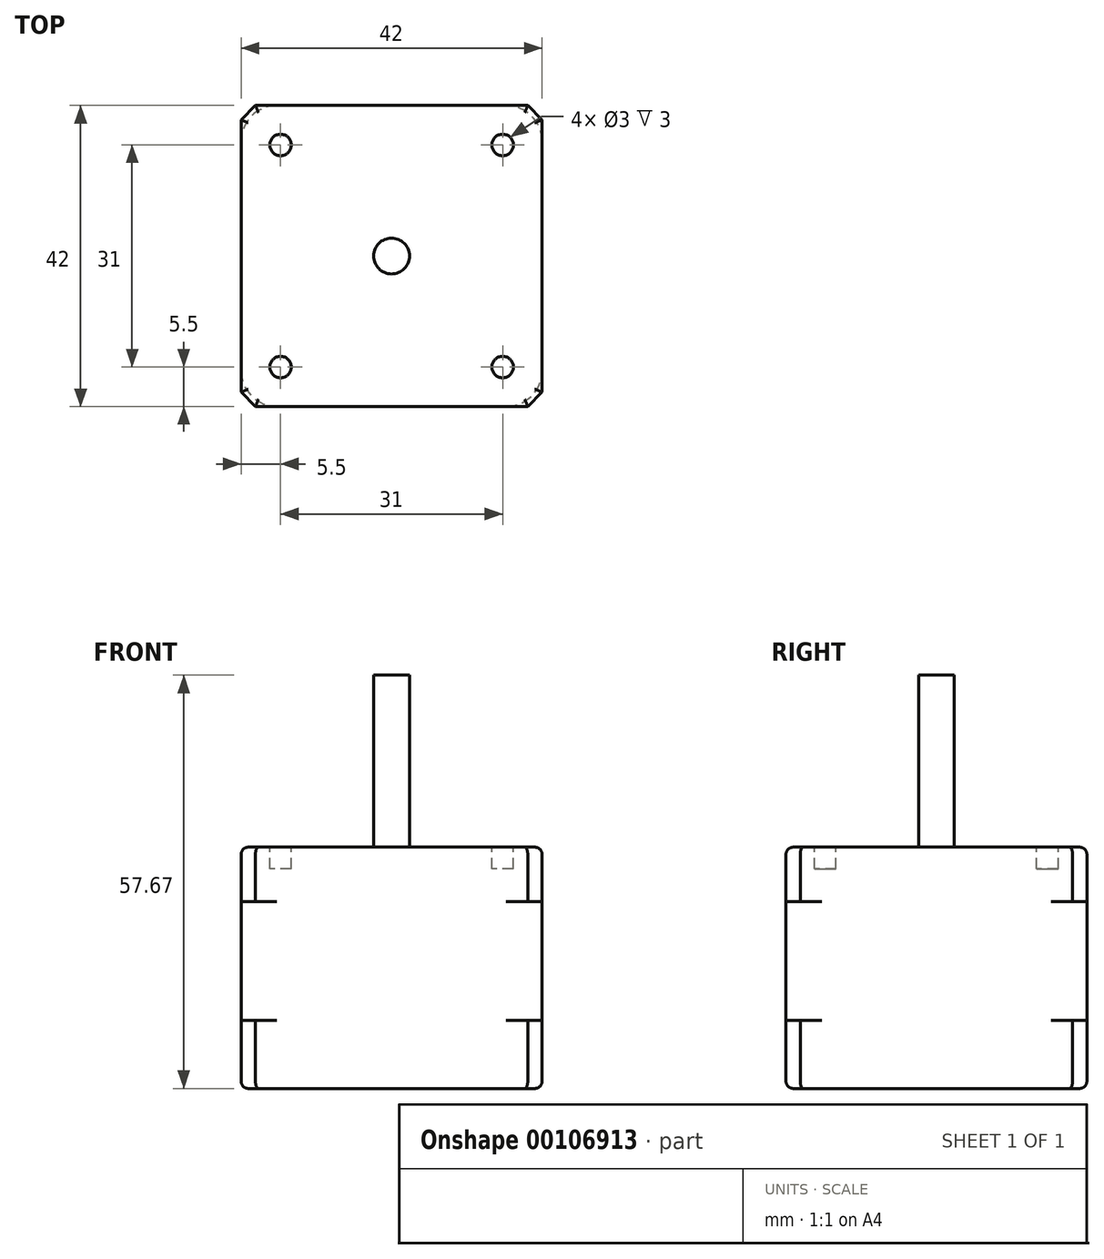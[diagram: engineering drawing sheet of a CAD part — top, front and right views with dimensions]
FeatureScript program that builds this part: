
annotation { "Feature Type Name" : "Feature", "Feature Type Description" : "" }
export const myFeature = defineFeature(function(context is Context, id is Id, definition is map)
    precondition{}
    {
        {
            var Q0;
            Q0=qCreatedBy(makeId("Top.planeOp"),FACE);
            var sketch = newSketch(context, id + "F0", { "sketchPlane" : qUnion([Q0])});
            skLineSegment(sketch, "E0.bottom", {"start": v(21, -21) * mm, "end": v(-21, -21) * mm});
            skLineSegment(sketch, "E0.top", {"start": v(21, 21) * mm, "end": v(-21, 21) * mm});
            skLineSegment(sketch, "E0.left", {"start": v(21, -21) * mm, "end": v(21, 21) * mm});
            skLineSegment(sketch, "E0.right", {"start": v(-21, -21) * mm, "end": v(-21, 21) * mm});
            skPoint(sketch, "E0.middle", {"position": v(0, 0) * mm});
            skSolve(sketch);
        }
        {
            var Q0;
            Q0 = qSketchRegion(id + "F0", true);
            extrude(context, id + "F1", {"entities" : qUnion([Q0]), "depth" : 9.5 * mm});
        }
        {
            var Q0;
            Q0=makeQuery(id+"F1.opExtrude","CAP_FACE",FACE,{"disambiguationData":[OSD([sQuery(id+"F0.wireOp",EDGE,"E0.bottom"),sQuery(id+"F0.wireOp",EDGE,"E0.top"),sQuery(id+"F0.wireOp",EDGE,"E0.left"),sQuery(id+"F0.wireOp",EDGE,"E0.right")])],"isStart":false});
            var sketch = newSketch(context, id + "F2", { "sketchPlane" : qUnion([Q0])});
            skLineSegment(sketch, "E1.bottom", {"start": v(16, -21) * mm, "end": v(-16, -21) * mm});
            skLineSegment(sketch, "E1.top", {"start": v(16, 21) * mm, "end": v(-16, 21) * mm});
            skLineSegment(sketch, "E1.left", {"start": v(21, -16) * mm, "end": v(21, 16) * mm});
            skLineSegment(sketch, "E1.right", {"start": v(-21, -16) * mm, "end": v(-21, 16) * mm});
            skPoint(sketch, "E1.middle", {"position": v(0, 0) * mm});
            skPoint(sketch, "E2.visualSharp", {"position": v(-21, 21) * mm});
            skArc(sketch, "E2.filletArc", {"start": v(-16, 21) * mm, "mid": v(-19.54, 19.54) * mm, "end": v(-21, 16) * mm});
            skPoint(sketch, "E3.visualSharp", {"position": v(-21, -21) * mm});
            skArc(sketch, "E3.filletArc", {"start": v(-21, -16) * mm, "mid": v(-19.54, -19.54) * mm, "end": v(-16, -21) * mm});
            skPoint(sketch, "E4.visualSharp", {"position": v(21, -21) * mm});
            skArc(sketch, "E4.filletArc", {"start": v(16, -21) * mm, "mid": v(19.54, -19.54) * mm, "end": v(21, -16) * mm});
            skPoint(sketch, "E5.visualSharp", {"position": v(21, 21) * mm});
            skArc(sketch, "E5.filletArc", {"start": v(21, 16) * mm, "mid": v(19.54, 19.54) * mm, "end": v(16, 21) * mm});
            skSolve(sketch);
        }
        {
            var Q0;
            Q0 = qSketchRegion(id + "F2", true);
            extrude(context, id + "F3", {"entities" : qUnion([Q0]), "operationType" : NewBodyOperationType.ADD, "depth" : 16.57 * mm});
        }
        {
            var Q0;
            Q0=makeQuery(id+"F3.opExtrude","CAP_FACE",FACE,{"disambiguationData":[OSD([sQuery(id+"F2.wireOp",EDGE,"E1.bottom"),sQuery(id+"F2.wireOp",EDGE,"E1.top"),sQuery(id+"F2.wireOp",EDGE,"E1.left"),sQuery(id+"F2.wireOp",EDGE,"E1.right"),sQuery(id+"F2.wireOp",EDGE,"E2.filletArc"),sQuery(id+"F2.wireOp",EDGE,"E3.filletArc"),sQuery(id+"F2.wireOp",EDGE,"E4.filletArc"),sQuery(id+"F2.wireOp",EDGE,"E5.filletArc")])],"isStart":false});
            var sketch = newSketch(context, id + "F4", { "sketchPlane" : qUnion([Q0])});
            skLineSegment(sketch, "E6.bottom", {"start": v(21, -21) * mm, "end": v(-21, -21) * mm});
            skLineSegment(sketch, "E6.top", {"start": v(21, 21) * mm, "end": v(-21, 21) * mm});
            skLineSegment(sketch, "E6.left", {"start": v(21, -21) * mm, "end": v(21, 21) * mm});
            skLineSegment(sketch, "E6.right", {"start": v(-21, -21) * mm, "end": v(-21, 21) * mm});
            skPoint(sketch, "E6.middle", {"position": v(0, 0) * mm});
            skSolve(sketch);
        }
        {
            var Q0;
            Q0 = qSketchRegion(id + "F4", true);
            extrude(context, id + "F5", {"entities" : qUnion([Q0]), "operationType" : NewBodyOperationType.ADD, "depth" : 7.6 * mm});
        }
        {
            var Q0;
            Q0=makeQuery(id+"F5.opExtrude","CAP_FACE",FACE,{"disambiguationData":[OSD([sQuery(id+"F4.wireOp",EDGE,"E6.bottom"),sQuery(id+"F4.wireOp",EDGE,"E6.top"),sQuery(id+"F4.wireOp",EDGE,"E6.left"),sQuery(id+"F4.wireOp",EDGE,"E6.right")])],"isStart":false});
            var sketch = newSketch(context, id + "F6", { "sketchPlane" : qUnion([Q0])});
            skLineSegment(sketch, "E7.bottom", {"start": v(15.5, -15.5) * mm, "end": v(14, -15.5) * mm});
            skLineSegment(sketch, "E7.top", {"start": v(15.5, 15.5) * mm, "end": v(14, 15.5) * mm});
            skLineSegment(sketch, "E7.left", {"start": v(15.5, -15.5) * mm, "end": v(15.5, -14) * mm});
            skLineSegment(sketch, "E7.right", {"start": v(-15.5, -15.5) * mm, "end": v(-15.5, -14) * mm});
            skPoint(sketch, "E7.middle", {"position": v(0, 0) * mm});
            skCircle(sketch, "E8", {"center": v(-15.5, 15.5) * mm, "radius": 1.5 * mm});
            skCircle(sketch, "E9", {"center": v(15.5, 15.5) * mm, "radius": 1.5 * mm});
            skCircle(sketch, "E10", {"center": v(-15.5, -15.5) * mm, "radius": 1.5 * mm});
            skCircle(sketch, "E11", {"center": v(15.5, -15.5) * mm, "radius": 1.5 * mm});
            skLineSegment(sketch, "E12.trimOffspring", {"start": v(-15.5, 14) * mm, "end": v(-15.5, 15.5) * mm});
            skLineSegment(sketch, "E13.trimOffspring", {"start": v(-14, 15.5) * mm, "end": v(-15.5, 15.5) * mm});
            skLineSegment(sketch, "E14.trimOffspring", {"start": v(15.5, 14) * mm, "end": v(15.5, 15.5) * mm});
            skLineSegment(sketch, "E15.trimOffspring", {"start": v(-14, -15.5) * mm, "end": v(-15.5, -15.5) * mm});
            skSolve(sketch);
        }
        {
            var Q0;
            Q0 = qSketchRegion(id + "F6", true);
            extrude(context, id + "F7", {"entities" : qUnion([Q0]), "operationType" : NewBodyOperationType.REMOVE, "oppositeDirection" : true, "depth" : 3 * mm});
        }
        {
            var Q0;
            Q0=makeQuery(id+"F5.opExtrude","CAP_FACE",FACE,{"disambiguationData":[OSD([sQuery(id+"F4.wireOp",EDGE,"E6.bottom"),sQuery(id+"F4.wireOp",EDGE,"E6.top"),sQuery(id+"F4.wireOp",EDGE,"E6.left"),sQuery(id+"F4.wireOp",EDGE,"E6.right")])],"isStart":false});
            var sketch = newSketch(context, id + "F8", { "sketchPlane" : qUnion([Q0])});
            skCircle(sketch, "E16", {"center": v(0, 0) * mm, "radius": 2.5 * mm});
            skSolve(sketch);
        }
        {
            var Q0;
            Q0 = qSketchRegion(id + "F8", true);
            extrude(context, id + "F9", {"entities" : qUnion([Q0]), "operationType" : NewBodyOperationType.ADD, "depth" : 24 * mm});
        }
        {
            var Q0;
            Q0=makeQuery(id+"F5.opExtrude","SWEPT_EDGE",EDGE,{"disambiguationData":[OSD([sQuery(id+"F4.wireOp",EDGE,"E6.top"),sQuery(id+"F4.wireOp",EDGE,"E6.left")])]});
            var Q1;
            Q1=makeQuery(id+"F1.opExtrude","SWEPT_EDGE",EDGE,{"disambiguationData":[OSD([sQuery(id+"F0.wireOp",EDGE,"E0.top"),sQuery(id+"F0.wireOp",EDGE,"E0.left")])]});
            var Q2;
            Q2=makeQuery(id+"F5.opExtrude","SWEPT_EDGE",EDGE,{"disambiguationData":[OSD([sQuery(id+"F4.wireOp",EDGE,"E6.top"),sQuery(id+"F4.wireOp",EDGE,"E6.right")])]});
            var Q3;
            Q3=makeQuery(id+"F1.opExtrude","SWEPT_EDGE",EDGE,{"disambiguationData":[OSD([sQuery(id+"F0.wireOp",EDGE,"E0.top"),sQuery(id+"F0.wireOp",EDGE,"E0.right")])]});
            var Q4;
            Q4=makeQuery(id+"F5.opExtrude","SWEPT_EDGE",EDGE,{"disambiguationData":[OSD([sQuery(id+"F4.wireOp",EDGE,"E6.bottom"),sQuery(id+"F4.wireOp",EDGE,"E6.right")])]});
            var Q5;
            Q5=makeQuery(id+"F1.opExtrude","SWEPT_EDGE",EDGE,{"disambiguationData":[OSD([sQuery(id+"F0.wireOp",EDGE,"E0.bottom"),sQuery(id+"F0.wireOp",EDGE,"E0.right")])]});
            var Q6;
            Q6=makeQuery(id+"F1.opExtrude","SWEPT_EDGE",EDGE,{"disambiguationData":[OSD([sQuery(id+"F0.wireOp",EDGE,"E0.bottom"),sQuery(id+"F0.wireOp",EDGE,"E0.left")])]});
            var Q7;
            Q7=makeQuery(id+"F5.opExtrude","SWEPT_EDGE",EDGE,{"disambiguationData":[OSD([sQuery(id+"F4.wireOp",EDGE,"E6.bottom"),sQuery(id+"F4.wireOp",EDGE,"E6.left")])]});
            chamfer(context, id + "F10", {"entities" : qUnion([Q0, Q1, Q2, Q3, Q4, Q5, Q6, Q7]), "width" : 2 * mm, "tangentPropagation" : true});
        }
        {
            var Q0;
            Q0=makeQuery(id+"F5.opExtrude","CAP_EDGE",EDGE,{"disambiguationData":[OSD([sQuery(id+"F4.wireOp",EDGE,"E6.top")])],"isStart":false});
            var Q1;
            {var subQ0=sQuery(id+"F4.wireOp",EDGE,"E6.right");var subQ1=sQuery(id+"F4.wireOp",EDGE,"E6.top");Q1=makeQuery(id+"F10.opChamfer","BLEND_EDGE",EDGE,{"blendedFrom":[makeQuery(id+"F5.opExtrude","SWEPT_EDGE",EDGE,{"disambiguationData":[OSD([subQ1,subQ0])]}),makeQuery(id+"F5.opExtrude","CAP_FACE",FACE,{"disambiguationData":[OSD([sQuery(id+"F4.wireOp",EDGE,"E6.bottom"),subQ1,sQuery(id+"F4.wireOp",EDGE,"E6.left"),subQ0])],"isStart":false})],"blendedInto":[makeQuery(id+"F5.opExtrude","CAP_FACE",FACE,{"disambiguationData":[OSD([sQuery(id+"F4.wireOp",EDGE,"E6.bottom"),subQ1,sQuery(id+"F4.wireOp",EDGE,"E6.left"),subQ0])],"isStart":false})]});}
            var Q2;
            Q2=makeQuery(id+"F5.opExtrude","CAP_EDGE",EDGE,{"disambiguationData":[OSD([sQuery(id+"F4.wireOp",EDGE,"E6.right")])],"isStart":false});
            var Q3;
            {var subQ0=sQuery(id+"F4.wireOp",EDGE,"E6.right");var subQ1=sQuery(id+"F4.wireOp",EDGE,"E6.bottom");Q3=makeQuery(id+"F10.opChamfer","BLEND_EDGE",EDGE,{"blendedFrom":[makeQuery(id+"F5.opExtrude","SWEPT_EDGE",EDGE,{"disambiguationData":[OSD([subQ1,subQ0])]}),makeQuery(id+"F5.opExtrude","CAP_FACE",FACE,{"disambiguationData":[OSD([subQ1,sQuery(id+"F4.wireOp",EDGE,"E6.top"),sQuery(id+"F4.wireOp",EDGE,"E6.left"),subQ0])],"isStart":false})],"blendedInto":[makeQuery(id+"F5.opExtrude","CAP_FACE",FACE,{"disambiguationData":[OSD([subQ1,sQuery(id+"F4.wireOp",EDGE,"E6.top"),sQuery(id+"F4.wireOp",EDGE,"E6.left"),subQ0])],"isStart":false})]});}
            var Q4;
            Q4=makeQuery(id+"F5.opExtrude","CAP_EDGE",EDGE,{"disambiguationData":[OSD([sQuery(id+"F4.wireOp",EDGE,"E6.bottom")])],"isStart":false});
            var Q5;
            {var subQ0=sQuery(id+"F4.wireOp",EDGE,"E6.left");var subQ1=sQuery(id+"F4.wireOp",EDGE,"E6.bottom");Q5=makeQuery(id+"F10.opChamfer","BLEND_EDGE",EDGE,{"blendedFrom":[makeQuery(id+"F5.opExtrude","SWEPT_EDGE",EDGE,{"disambiguationData":[OSD([subQ1,subQ0])]}),makeQuery(id+"F5.opExtrude","CAP_FACE",FACE,{"disambiguationData":[OSD([subQ1,sQuery(id+"F4.wireOp",EDGE,"E6.top"),subQ0,sQuery(id+"F4.wireOp",EDGE,"E6.right")])],"isStart":false})],"blendedInto":[makeQuery(id+"F5.opExtrude","CAP_FACE",FACE,{"disambiguationData":[OSD([subQ1,sQuery(id+"F4.wireOp",EDGE,"E6.top"),subQ0,sQuery(id+"F4.wireOp",EDGE,"E6.right")])],"isStart":false})]});}
            var Q6;
            Q6=makeQuery(id+"F5.opExtrude","CAP_EDGE",EDGE,{"disambiguationData":[OSD([sQuery(id+"F4.wireOp",EDGE,"E6.left")])],"isStart":false});
            var Q7;
            {var subQ0=sQuery(id+"F4.wireOp",EDGE,"E6.left");var subQ1=sQuery(id+"F4.wireOp",EDGE,"E6.top");Q7=makeQuery(id+"F10.opChamfer","BLEND_EDGE",EDGE,{"blendedFrom":[makeQuery(id+"F5.opExtrude","SWEPT_EDGE",EDGE,{"disambiguationData":[OSD([subQ1,subQ0])]}),makeQuery(id+"F5.opExtrude","CAP_FACE",FACE,{"disambiguationData":[OSD([sQuery(id+"F4.wireOp",EDGE,"E6.bottom"),subQ1,subQ0,sQuery(id+"F4.wireOp",EDGE,"E6.right")])],"isStart":false})],"blendedInto":[makeQuery(id+"F5.opExtrude","CAP_FACE",FACE,{"disambiguationData":[OSD([sQuery(id+"F4.wireOp",EDGE,"E6.bottom"),subQ1,subQ0,sQuery(id+"F4.wireOp",EDGE,"E6.right")])],"isStart":false})]});}
            var Q8;
            Q8=makeQuery(id+"F1.opExtrude","CAP_EDGE",EDGE,{"disambiguationData":[OSD([sQuery(id+"F0.wireOp",EDGE,"E0.top")])],"isStart":true});
            var Q9;
            Q9=makeQuery(id+"F1.opExtrude","CAP_EDGE",EDGE,{"disambiguationData":[OSD([sQuery(id+"F0.wireOp",EDGE,"E0.left")])],"isStart":true});
            var Q10;
            {var subQ0=sQuery(id+"F0.wireOp",EDGE,"E0.left");var subQ1=sQuery(id+"F0.wireOp",EDGE,"E0.top");Q10=makeQuery(id+"F10.opChamfer","BLEND_EDGE",EDGE,{"blendedFrom":[makeQuery(id+"F1.opExtrude","SWEPT_EDGE",EDGE,{"disambiguationData":[OSD([subQ1,subQ0])]}),makeQuery(id+"F1.opExtrude","CAP_FACE",FACE,{"disambiguationData":[OSD([sQuery(id+"F0.wireOp",EDGE,"E0.bottom"),subQ1,subQ0,sQuery(id+"F0.wireOp",EDGE,"E0.right")])],"isStart":true})],"blendedInto":[makeQuery(id+"F1.opExtrude","CAP_FACE",FACE,{"disambiguationData":[OSD([sQuery(id+"F0.wireOp",EDGE,"E0.bottom"),subQ1,subQ0,sQuery(id+"F0.wireOp",EDGE,"E0.right")])],"isStart":true})]});}
            var Q11;
            Q11=makeQuery(id+"F1.opExtrude","CAP_EDGE",EDGE,{"disambiguationData":[OSD([sQuery(id+"F0.wireOp",EDGE,"E0.right")])],"isStart":true});
            var Q12;
            {var subQ0=sQuery(id+"F0.wireOp",EDGE,"E0.right");var subQ1=sQuery(id+"F0.wireOp",EDGE,"E0.top");Q12=makeQuery(id+"F10.opChamfer","BLEND_EDGE",EDGE,{"blendedFrom":[makeQuery(id+"F1.opExtrude","SWEPT_EDGE",EDGE,{"disambiguationData":[OSD([subQ1,subQ0])]}),makeQuery(id+"F1.opExtrude","CAP_FACE",FACE,{"disambiguationData":[OSD([sQuery(id+"F0.wireOp",EDGE,"E0.bottom"),subQ1,sQuery(id+"F0.wireOp",EDGE,"E0.left"),subQ0])],"isStart":true})],"blendedInto":[makeQuery(id+"F1.opExtrude","CAP_FACE",FACE,{"disambiguationData":[OSD([sQuery(id+"F0.wireOp",EDGE,"E0.bottom"),subQ1,sQuery(id+"F0.wireOp",EDGE,"E0.left"),subQ0])],"isStart":true})]});}
            var Q13;
            Q13=makeQuery(id+"F1.opExtrude","CAP_EDGE",EDGE,{"disambiguationData":[OSD([sQuery(id+"F0.wireOp",EDGE,"E0.bottom")])],"isStart":true});
            var Q14;
            {var subQ0=sQuery(id+"F0.wireOp",EDGE,"E0.left");var subQ1=sQuery(id+"F0.wireOp",EDGE,"E0.bottom");Q14=makeQuery(id+"F10.opChamfer","BLEND_EDGE",EDGE,{"blendedFrom":[makeQuery(id+"F1.opExtrude","SWEPT_EDGE",EDGE,{"disambiguationData":[OSD([subQ1,subQ0])]}),makeQuery(id+"F1.opExtrude","CAP_FACE",FACE,{"disambiguationData":[OSD([subQ1,sQuery(id+"F0.wireOp",EDGE,"E0.top"),subQ0,sQuery(id+"F0.wireOp",EDGE,"E0.right")])],"isStart":true})],"blendedInto":[makeQuery(id+"F1.opExtrude","CAP_FACE",FACE,{"disambiguationData":[OSD([subQ1,sQuery(id+"F0.wireOp",EDGE,"E0.top"),subQ0,sQuery(id+"F0.wireOp",EDGE,"E0.right")])],"isStart":true})]});}
            var Q15;
            {var subQ0=sQuery(id+"F0.wireOp",EDGE,"E0.right");var subQ1=sQuery(id+"F0.wireOp",EDGE,"E0.bottom");Q15=makeQuery(id+"F10.opChamfer","BLEND_EDGE",EDGE,{"blendedFrom":[makeQuery(id+"F1.opExtrude","SWEPT_EDGE",EDGE,{"disambiguationData":[OSD([subQ1,subQ0])]}),makeQuery(id+"F1.opExtrude","CAP_FACE",FACE,{"disambiguationData":[OSD([subQ1,sQuery(id+"F0.wireOp",EDGE,"E0.top"),sQuery(id+"F0.wireOp",EDGE,"E0.left"),subQ0])],"isStart":true})],"blendedInto":[makeQuery(id+"F1.opExtrude","CAP_FACE",FACE,{"disambiguationData":[OSD([subQ1,sQuery(id+"F0.wireOp",EDGE,"E0.top"),sQuery(id+"F0.wireOp",EDGE,"E0.left"),subQ0])],"isStart":true})]});}
            fillet(context, id + "F11", {"entities" : qUnion([Q0, Q1, Q2, Q3, Q4, Q5, Q6, Q7, Q8, Q9, Q10, Q11, Q12, Q13, Q14, Q15]), "radius" : 1 * mm, "tangentPropagation" : true, "allowEdgeOverflow" : false});
        }
    });
